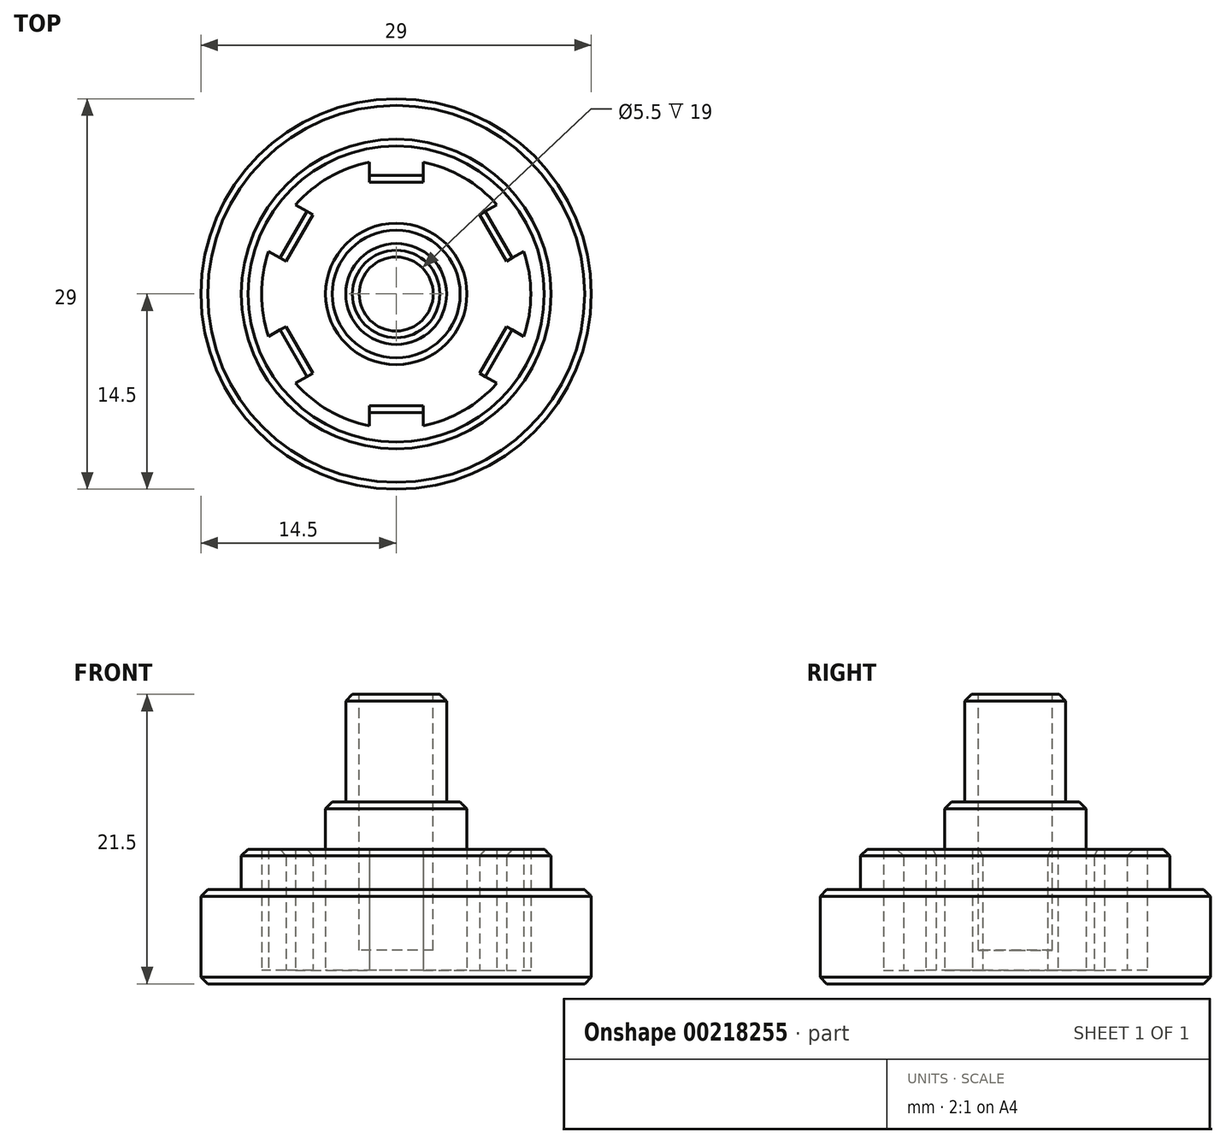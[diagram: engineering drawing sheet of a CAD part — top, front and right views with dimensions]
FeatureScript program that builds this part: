
annotation { "Feature Type Name" : "Feature", "Feature Type Description" : "" }
export const myFeature = defineFeature(function(context is Context, id is Id, definition is map)
    precondition{}
    {
        {
            var Q0;
            Q0=qCreatedBy(makeId("Top.planeOp"),FACE);
            var sketch = newSketch(context, id + "F0", { "sketchPlane" : qUnion([Q0])});
            skCircle(sketch, "E0", {"center": v(0, 0) * mm, "radius": 14.5 * mm});
            skSolve(sketch);
        }
        {
            var Q0;
            Q0=qSketchRegion(id+"F0",true);
            extrude(context, id + "F1", {"entities" : qUnion([Q0]), "depth" : 10 * mm});
        }
        {
            var Q0;
            Q0=makeQuery(id+"F1.opExtrude","CAP_FACE",FACE,{"disambiguationData":[OSD([sQuery(id+"F0.wireOp",EDGE,"E0")])],"isStart":false});
            var sketch = newSketch(context, id + "F2", { "sketchPlane" : qUnion([Q0])});
            skArc(sketch, "E1", {"start": v(-2, 9.8) * mm, "mid": v(-5, 8.66) * mm, "end": v(-7.49, 6.63) * mm});
            skCircle(sketch, "E2", {"center": v(0, 0) * mm, "radius": 11.5 * mm});
            skLineSegment(sketch, "E3", {"start": v(-2, 9.8) * mm, "end": v(-2, 8.3) * mm});
            skLineSegment(sketch, "E4", {"start": v(-2, 8.3) * mm, "end": v(2, 8.3) * mm});
            skLineSegment(sketch, "E5", {"start": v(2, 8.3) * mm, "end": v(2, 9.8) * mm});
            skLineSegment(sketch, "E6.1.0", {"start": v(-8.19, 2.42) * mm, "end": v(-6.19, 5.88) * mm});
            skLineSegment(sketch, "E6.1.1", {"start": v(-6.19, 5.88) * mm, "end": v(-7.49, 6.63) * mm});
            skLineSegment(sketch, "E6.1.2", {"start": v(-9.49, 3.17) * mm, "end": v(-8.19, 2.42) * mm});
            skLineSegment(sketch, "E6.2.0", {"start": v(-6.19, -5.88) * mm, "end": v(-8.19, -2.42) * mm});
            skLineSegment(sketch, "E6.2.1", {"start": v(-8.19, -2.42) * mm, "end": v(-9.49, -3.17) * mm});
            skLineSegment(sketch, "E6.2.2", {"start": v(-7.49, -6.63) * mm, "end": v(-6.19, -5.88) * mm});
            skLineSegment(sketch, "E6.3.0", {"start": v(2, -8.3) * mm, "end": v(-2, -8.3) * mm});
            skLineSegment(sketch, "E6.3.1", {"start": v(-2, -8.3) * mm, "end": v(-2, -9.8) * mm});
            skLineSegment(sketch, "E6.3.2", {"start": v(2, -9.8) * mm, "end": v(2, -8.3) * mm});
            skLineSegment(sketch, "E6.4.0", {"start": v(8.19, -2.42) * mm, "end": v(6.19, -5.88) * mm});
            skLineSegment(sketch, "E6.4.1", {"start": v(6.19, -5.88) * mm, "end": v(7.49, -6.63) * mm});
            skLineSegment(sketch, "E6.4.2", {"start": v(9.49, -3.17) * mm, "end": v(8.19, -2.42) * mm});
            skLineSegment(sketch, "E6.5.0", {"start": v(6.19, 5.88) * mm, "end": v(8.19, 2.42) * mm});
            skLineSegment(sketch, "E6.5.1", {"start": v(8.19, 2.42) * mm, "end": v(9.49, 3.17) * mm});
            skLineSegment(sketch, "E6.5.2", {"start": v(7.49, 6.63) * mm, "end": v(6.19, 5.88) * mm});
            skArc(sketch, "E7.trimOffspring", {"start": v(7.49, 6.63) * mm, "mid": v(5, 8.66) * mm, "end": v(2, 9.8) * mm});
            skArc(sketch, "E8.trimOffspring", {"start": v(9.49, -3.17) * mm, "mid": v(10, 0) * mm, "end": v(9.49, 3.17) * mm});
            skArc(sketch, "E9.trimOffspring", {"start": v(2, -9.8) * mm, "mid": v(5, -8.66) * mm, "end": v(7.49, -6.63) * mm});
            skArc(sketch, "E10.trimOffspring", {"start": v(-7.49, -6.63) * mm, "mid": v(-5, -8.66) * mm, "end": v(-2, -9.8) * mm});
            skArc(sketch, "E11.trimOffspring", {"start": v(-9.49, 3.17) * mm, "mid": v(-10, 0) * mm, "end": v(-9.49, -3.17) * mm});
            skSolve(sketch);
        }
        {
            var Q0;
            Q0=qSketchRegion(id+"F2",true);
            extrude(context, id + "F3", {"entities" : qUnion([Q0]), "operationType" : NewBodyOperationType.ADD, "depth" : 9 * mm});
        }
        {
            var Q0;
            Q0=makeQuery(id+"F3.opExtrude","CAP_EDGE",EDGE,{"disambiguationData":[OSD([sQuery(id+"F2.wireOp",EDGE,"E4")])],"isStart":false});
            var Q1;
            Q1=makeQuery(id+"F3.opExtrude","CAP_EDGE",EDGE,{"disambiguationData":[OSD([sQuery(id+"F2.wireOp",EDGE,"E6.1.0")])],"isStart":false});
            var Q2;
            Q2=makeQuery(id+"F3.opExtrude","CAP_EDGE",EDGE,{"disambiguationData":[OSD([sQuery(id+"F2.wireOp",EDGE,"E6.2.0")])],"isStart":false});
            var Q3;
            Q3=makeQuery(id+"F3.opExtrude","CAP_EDGE",EDGE,{"disambiguationData":[OSD([sQuery(id+"F2.wireOp",EDGE,"E6.3.0")])],"isStart":false});
            var Q4;
            Q4=makeQuery(id+"F3.opExtrude","CAP_EDGE",EDGE,{"disambiguationData":[OSD([sQuery(id+"F2.wireOp",EDGE,"E6.4.0")])],"isStart":false});
            var Q5;
            Q5=makeQuery(id+"F3.opExtrude","CAP_EDGE",EDGE,{"disambiguationData":[OSD([sQuery(id+"F2.wireOp",EDGE,"E6.5.0")])],"isStart":false});
            chamfer(context, id + "F4", {"entities" : qUnion([Q0, Q1, Q2, Q3, Q4, Q5]), "width" : .5 * mm, "tangentPropagation" : true});
        }
        {
            var Q0;
            Q0=makeQuery(id+"F3.boolean.opBoolean","SPLIT",FACE,{"disambiguationData":[TD([makeQuery(id+"F3.opExtrude","SWEPT_FACE",FACE,{"disambiguationData":[OSD([sQuery(id+"F2.wireOp",EDGE,"E1")])]})])],"derivedFrom":makeQuery(id+"F1.opExtrude","CAP_FACE",FACE,{"disambiguationData":[OSD([sQuery(id+"F0.wireOp",EDGE,"E0")])],"isStart":false})});
            var sketch = newSketch(context, id + "F5", { "sketchPlane" : qUnion([Q0])});
            skCircle(sketch, "E12", {"center": v(0, 0) * mm, "radius": 5.25 * mm});
            skSolve(sketch);
        }
        {
            var Q0;
            Q0=qSketchRegion(id+"F5",true);
            extrude(context, id + "F6", {"entities" : qUnion([Q0]), "operationType" : NewBodyOperationType.ADD, "depth" : 12.5 * mm});
        }
        {
            var Q0;
            Q0=makeQuery(id+"F6.opExtrude","CAP_EDGE",EDGE,{"disambiguationData":[OSD([sQuery(id+"F5.wireOp",EDGE,"E12")])],"isStart":false});
            chamfer(context, id + "F7", {"entities" : qUnion([Q0]), "width" : .5 * mm, "tangentPropagation" : true});
        }
        {
            var Q0;
            Q0=makeQuery(id+"F6.opExtrude","CAP_FACE",FACE,{"disambiguationData":[OSD([sQuery(id+"F5.wireOp",EDGE,"E12")])],"isStart":false});
            var sketch = newSketch(context, id + "F8", { "sketchPlane" : qUnion([Q0])});
            skCircle(sketch, "E13", {"center": v(0, 0) * mm, "radius": 3.75 * mm});
            skSolve(sketch);
        }
        {
            var Q0;
            Q0=qSketchRegion(id+"F8",true);
            extrude(context, id + "F9", {"entities" : qUnion([Q0]), "operationType" : NewBodyOperationType.ADD, "depth" : 8 * mm});
        }
        {
            var Q0;
            Q0=makeQuery(id+"F9.opExtrude","CAP_EDGE",EDGE,{"disambiguationData":[OSD([sQuery(id+"F8.wireOp",EDGE,"E13")])],"isStart":false});
            chamfer(context, id + "F10", {"entities" : qUnion([Q0]), "width" : .5 * mm, "tangentPropagation" : true});
        }
        {
            var Q0;
            {var subQ0=sQuery(id+"F0.wireOp",EDGE,"E0");Q0=makeQuery(id+"F3.boolean.opBoolean","SPLIT",FACE,{"disambiguationData":[TD([makeQuery(id+"F1.opExtrude","SWEPT_FACE",FACE,{"disambiguationData":[OSD([subQ0])]})])],"derivedFrom":makeQuery(id+"F1.opExtrude","CAP_FACE",FACE,{"disambiguationData":[OSD([subQ0])],"isStart":false})});}
            var sketch = newSketch(context, id + "F11", { "sketchPlane" : qUnion([Q0])});
            skCircle(sketch, "E14", {"center": v(0, 0) * mm, "radius": 14.5 * mm});
            skCircle(sketch, "E15", {"center": v(0, 0) * mm, "radius": 11.5 * mm});
            skSolve(sketch);
        }
        {
            var Q0;
            Q0=qSketchRegion(id+"F11",true);
            extrude(context, id + "F12", {"entities" : qUnion([Q0]), "operationType" : NewBodyOperationType.ADD, "depth" : 6 * mm});
        }
        {
            var Q0;
            Q0=makeQuery(id+"F1.opExtrude","CAP_FACE",FACE,{"disambiguationData":[OSD([sQuery(id+"F0.wireOp",EDGE,"E0")])],"isStart":true});
            var sketch = newSketch(context, id + "F13", { "sketchPlane" : qUnion([Q0])});
            skCircle(sketch, "E16", {"center": v(0, 0) * mm, "radius": 25 * mm});
            skSolve(sketch);
        }
        {
            var Q0;
            Q0=qSketchRegion(id+"F13",true);
            extrude(context, id + "F14", {"entities" : qUnion([Q0]), "operationType" : NewBodyOperationType.REMOVE, "oppositeDirection" : true, "depth" : 9 * mm});
        }
        {
            var Q0;
            Q0=makeQuery(id+"F3.opExtrude","CAP_EDGE",EDGE,{"disambiguationData":[OSD([sQuery(id+"F2.wireOp",EDGE,"E2")])],"isStart":false});
            var Q1;
            Q1=makeQuery(id+"F12.opExtrude","CAP_EDGE",EDGE,{"disambiguationData":[OSD([sQuery(id+"F11.wireOp",EDGE,"E14")])],"isStart":false});
            var Q2;
            Q2=makeQuery(id+"F14.boolean.opBoolean","COPY",EDGE,{"derivedFrom":makeQuery(id+"F14.opExtrude","CAP_EDGE",EDGE,{"disambiguationData":[OSD([sQuery(id+"F13.wireOp",EDGE,"E16")])],"isStart":false})});
            var Q3;
            Q3=makeQuery(id+"F14.boolean.opBoolean","INTERSECT",EDGE,{"derivedFrom":[makeQuery(id+"F12.boolean.opBoolean","MERGE",FACE,{"derivedFrom":[makeQuery(id+"F1.opExtrude","SWEPT_FACE",FACE,{"disambiguationData":[OSD([sQuery(id+"F0.wireOp",EDGE,"E0")])]}),makeQuery(id+"F12.opExtrude","SWEPT_FACE",FACE,{"disambiguationData":[OSD([sQuery(id+"F11.wireOp",EDGE,"E14")])]})]}),makeQuery(id+"F14.opExtrude","CAP_FACE",FACE,{"disambiguationData":[OSD([sQuery(id+"F13.wireOp",EDGE,"E16")])],"isStart":false})]});
            chamfer(context, id + "F15", {"entities" : qUnion([Q0, Q1, Q2, Q3]), "width" : .5 * mm, "tangentPropagation" : true});
        }
        {
            var Q0;
            Q0=makeQuery(id+"F9.opExtrude","CAP_FACE",FACE,{"disambiguationData":[OSD([sQuery(id+"F8.wireOp",EDGE,"E13")])],"isStart":false});
            var sketch = newSketch(context, id + "F16", { "sketchPlane" : qUnion([Q0])});
            skCircle(sketch, "E17", {"center": v(0, 0) * mm, "radius": 2.75 * mm});
            skSolve(sketch);
        }
        {
            var Q0;
            Q0 = qSketchRegion(id + "F16", true);
            extrude(context, id + "F17", {"entities" : qUnion([Q0]), "operationType" : NewBodyOperationType.REMOVE, "oppositeDirection" : true, "depth" : 19 * mm});
        }
    });
